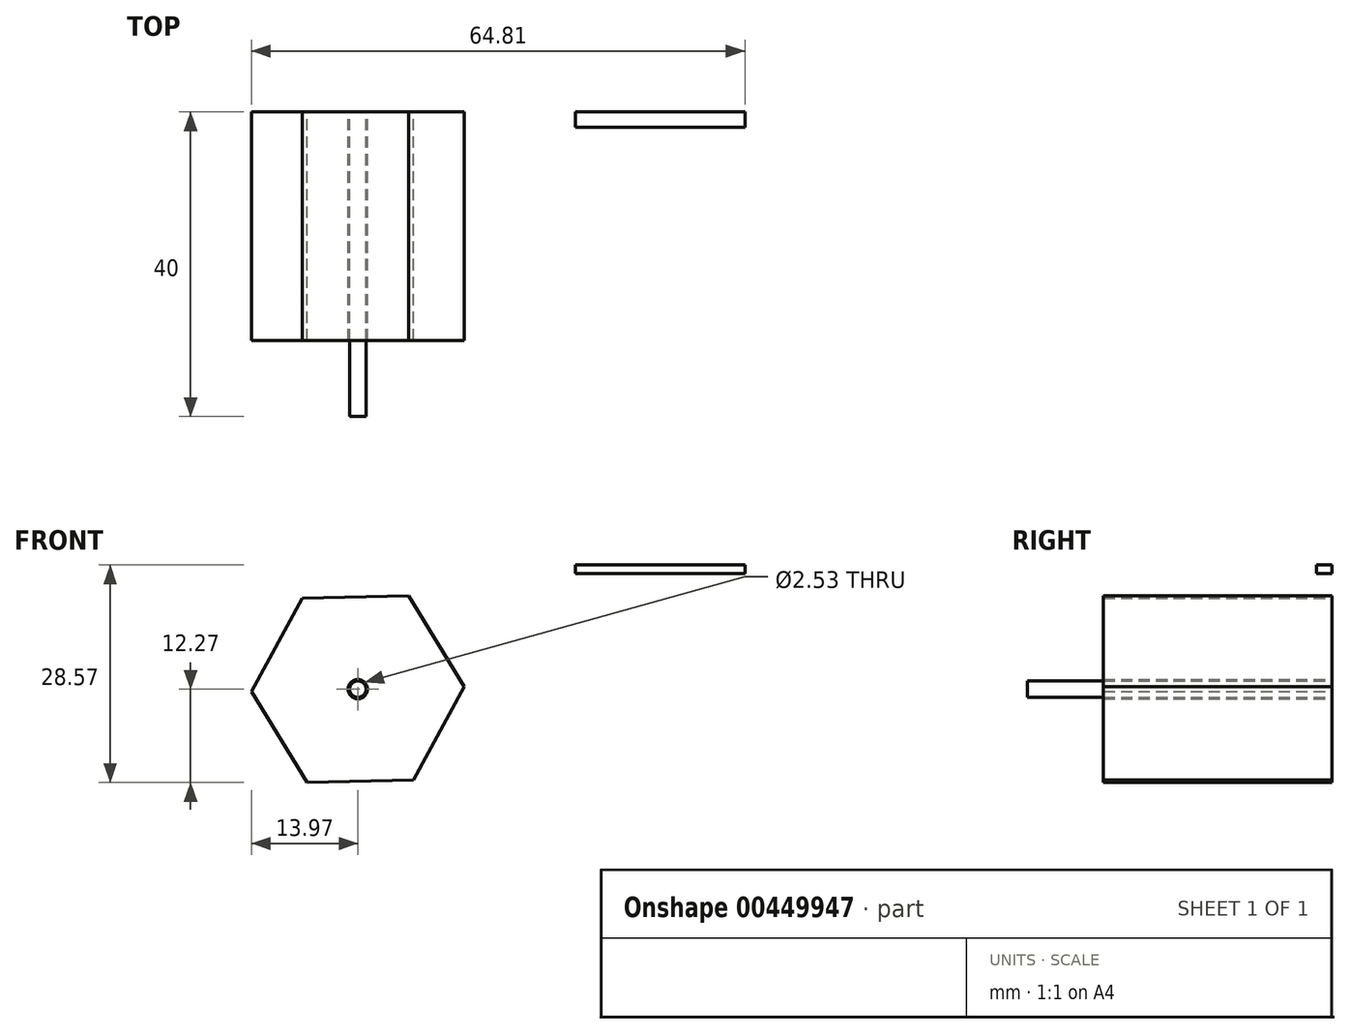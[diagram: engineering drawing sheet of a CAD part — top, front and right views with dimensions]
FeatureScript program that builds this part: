
annotation { "Feature Type Name" : "Feature", "Feature Type Description" : "" }
export const myFeature = defineFeature(function(context is Context, id is Id, definition is map)
    precondition{}
    {
        {
            var Q0;
            Q0=qCreatedBy(makeId("Front.planeOp"),FACE);
            var sketch = newSketch(context, id + "F0", { "sketchPlane" : qUnion([Q0])});
            skCircle(sketch, "E0.cCircle", {"center": v(0, 0) * mm, "radius": 12.1 * mm, "construction": true});
            skLineSegment(sketch, "E0.0", {"start": v(13.97, 0.34) * mm, "end": v(7.28, -11.93) * mm});
            skLineSegment(sketch, "E0.1", {"start": v(7.28, -11.93) * mm, "end": v(-6.7, -12.27) * mm});
            skLineSegment(sketch, "E0.2", {"start": v(-6.7, -12.27) * mm, "end": v(-13.97, -0.34) * mm});
            skLineSegment(sketch, "E0.3", {"start": v(-13.97, -0.34) * mm, "end": v(-7.28, 11.93) * mm});
            skLineSegment(sketch, "E0.4", {"start": v(-7.28, 11.93) * mm, "end": v(6.7, 12.27) * mm});
            skLineSegment(sketch, "E0.5", {"start": v(6.7, 12.27) * mm, "end": v(13.97, 0.34) * mm});
            skPoint(sketch, "E0.0.midPoint", {"position": v(10.63, -5.8) * mm});
            skCircle(sketch, "E1", {"center": v(0, 0) * mm, "radius": 1.27 * mm});
            skSolve(sketch);
        }
        {
            var Q0;
            Q0=makeQuery(id+"F0.imprint","IMPRINT",FACE,{"disambiguationData":[TD([[makeQuery(id+"F0.imprint","IMPRINT",EDGE,{"derivedFrom":sQuery(id+"F0.wireOp",EDGE,"E0.0")}),-1.0]])]});
            extrude(context, id + "F1", {"entities" : qUnion([Q0]), "depth" : 30 * mm});
        }
        {
            var Q0;
            Q0=qCreatedBy(makeId("Front.planeOp"),FACE);
            var sketch = newSketch(context, id + "F2", { "sketchPlane" : qUnion([Q0])});
            skCircle(sketch, "E2", {"center": v(0, 0) * mm, "radius": 1.08 * mm});
            skSolve(sketch);
        }
        {
            var Q0;
            Q0=makeQuery(id+"F2.imprint","IMPRINT",FACE,{"disambiguationData":[TD([[makeQuery(id+"F2.imprint","IMPRINT",EDGE,{"derivedFrom":sQuery(id+"F2.wireOp",EDGE,"E2")}),1.0]])]});
            extrude(context, id + "F3", {"entities" : qUnion([Q0]), "depth" : 40 * mm});
        }
        {
            var Q0;
            Q0=qCreatedBy(makeId("Front.planeOp"),FACE);
            var sketch = newSketch(context, id + "F4", { "sketchPlane" : qUnion([Q0])});
            skLineSegment(sketch, "E3.bottom", {"start": v(28.54, 16.3) * mm, "end": v(50.84, 16.3) * mm});
            skLineSegment(sketch, "E3.top", {"start": v(28.54, 15.16) * mm, "end": v(50.84, 15.16) * mm});
            skLineSegment(sketch, "E3.left", {"start": v(28.54, 16.3) * mm, "end": v(28.54, 15.16) * mm});
            skLineSegment(sketch, "E3.right", {"start": v(50.84, 16.3) * mm, "end": v(50.84, 15.16) * mm});
            skSolve(sketch);
        }
        {
            var Q0;
            Q0=makeQuery(id+"F4.imprint","IMPRINT",FACE,{"disambiguationData":[TD([[makeQuery(id+"F4.imprint","IMPRINT",EDGE,{"derivedFrom":sQuery(id+"F4.wireOp",EDGE,"E3.bottom")}),-1.0]])]});
            extrude(context, id + "F5", {"entities" : qUnion([Q0]), "depth" : 2 * mm});
        }
    });
